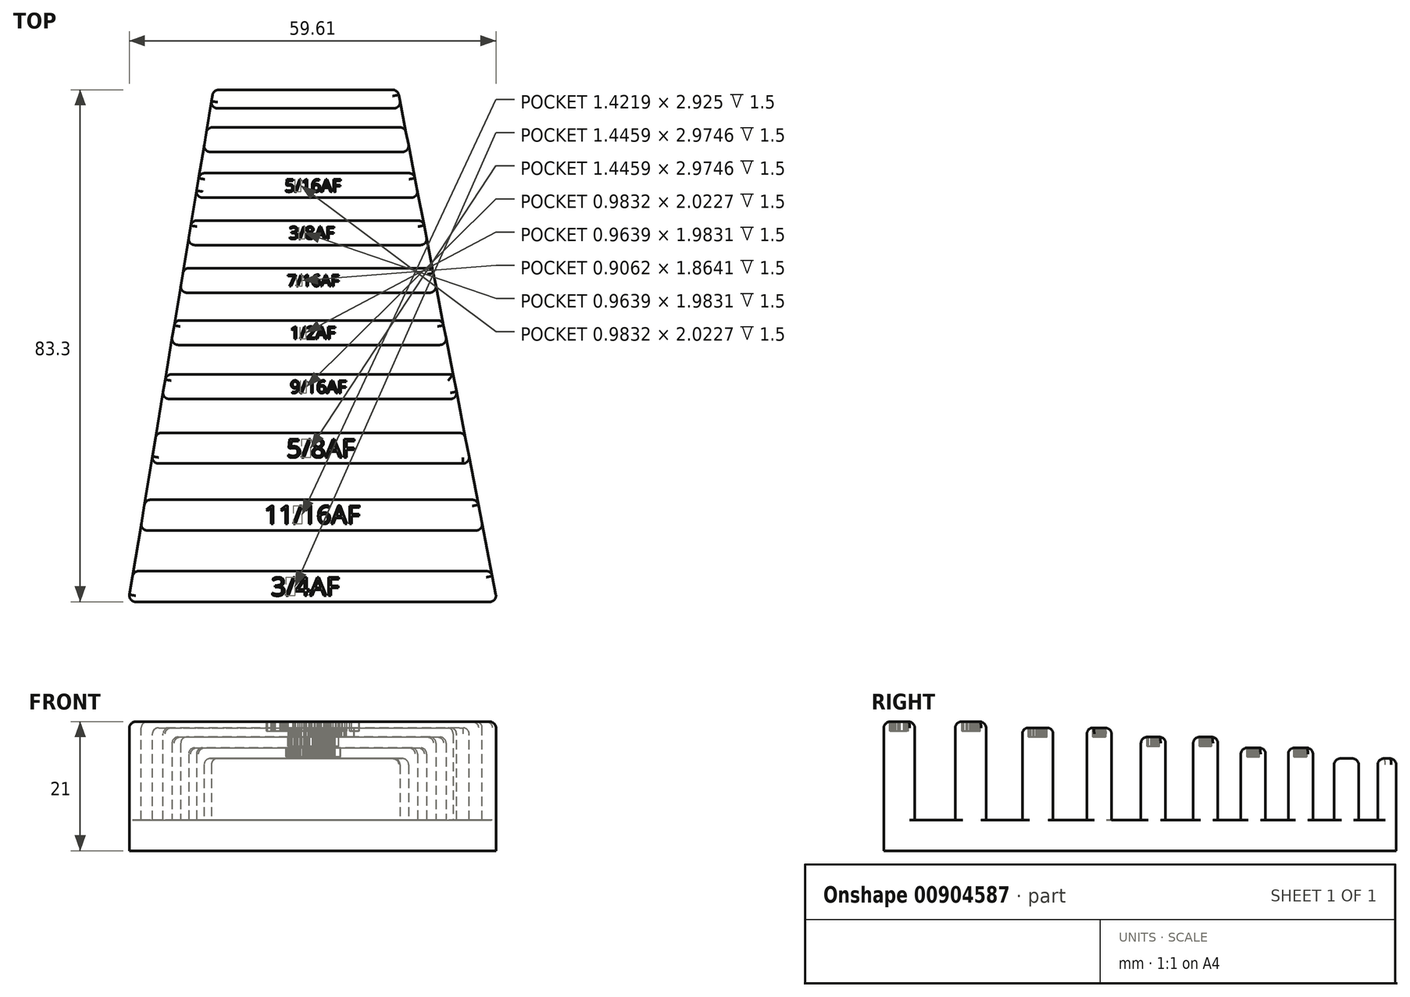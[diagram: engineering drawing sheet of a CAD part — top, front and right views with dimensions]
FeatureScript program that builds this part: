
annotation { "Feature Type Name" : "Feature", "Feature Type Description" : "" }
export const myFeature = defineFeature(function(context is Context, id is Id, definition is map)
    precondition{}
    {
        {
            var Q0;
            Q0=qCreatedBy(makeId("Top.planeOp"),FACE);
            var sketch = newSketch(context, id + "F0", { "sketchPlane" : qUnion([Q0])});
            skLineSegment(sketch, "E0.top", {"start": v(-30, -26.46) * mm, "end": v(30, -26.46) * mm});
            skLineSegment(sketch, "E1", {"start": v(-30, -26.46) * mm, "end": v(-16.18, 56.84) * mm});
            skLineSegment(sketch, "E2", {"start": v(-16.18, 56.84) * mm, "end": v(13.82, 56.84) * mm});
            skLineSegment(sketch, "E3", {"start": v(13.82, 56.84) * mm, "end": v(30, -26.46) * mm});
            skSolve(sketch);
        }
        {
            var Q0;
            Q0=qSketchRegion(id+"F0",true);
            extrude(context, id + "F1", {"entities" : qUnion([Q0]), "depth" : 5 * mm, "offsetDistance" : 25 * mm});
        }
        {
            var Q0;
            Q0=makeQuery(id+"F1.opExtrude","CAP_FACE",FACE,{"disambiguationData":[OSD([sQuery(id+"F0.wireOp",EDGE,"E0.top"),sQuery(id+"F0.wireOp",EDGE,"E1"),sQuery(id+"F0.wireOp",EDGE,"E2"),sQuery(id+"F0.wireOp",EDGE,"E3")])],"isStart":false});
            var sketch = newSketch(context, id + "F2", { "sketchPlane" : qUnion([Q0])});
            skLineSegment(sketch, "E4", {"start": v(-16.18, 56.84) * mm, "end": v(13.82, 56.84) * mm});
            skLineSegment(sketch, "E5", {"start": v(13.82, 56.84) * mm, "end": v(14.4, 53.84) * mm});
            skLineSegment(sketch, "E6", {"start": v(14.4, 53.84) * mm, "end": v(-16.68, 53.84) * mm});
            skLineSegment(sketch, "E7", {"start": v(-16.68, 53.84) * mm, "end": v(-16.18, 56.84) * mm});
            skLineSegment(sketch, "E8", {"start": v(-17.2, 50.74) * mm, "end": v(15, 50.74) * mm});
            skLineSegment(sketch, "E9", {"start": v(15, 50.74) * mm, "end": v(15.78, 46.74) * mm});
            skLineSegment(sketch, "E10", {"start": v(15.78, 46.74) * mm, "end": v(-17.85, 46.74) * mm});
            skLineSegment(sketch, "E11", {"start": v(-17.85, 46.74) * mm, "end": v(-17.2, 50.74) * mm});
            skLineSegment(sketch, "E12", {"start": v(-18.43, 43.3) * mm, "end": v(16.45, 43.3) * mm});
            skLineSegment(sketch, "E13", {"start": v(16.45, 43.3) * mm, "end": v(17.23, 39.3) * mm});
            skLineSegment(sketch, "E14", {"start": v(17.23, 39.3) * mm, "end": v(-19.1, 39.3) * mm});
            skLineSegment(sketch, "E15", {"start": v(-19.1, 39.3) * mm, "end": v(-18.43, 43.3) * mm});
            skLineSegment(sketch, "E16", {"start": v(-19.7, 35.6) * mm, "end": v(17.95, 35.6) * mm});
            skLineSegment(sketch, "E17", {"start": v(17.95, 35.6) * mm, "end": v(18.73, 31.6) * mm});
            skLineSegment(sketch, "E18", {"start": v(18.73, 31.6) * mm, "end": v(-20.37, 31.6) * mm});
            skLineSegment(sketch, "E19", {"start": v(-20.37, 31.6) * mm, "end": v(-19.7, 35.6) * mm});
            skLineSegment(sketch, "E20", {"start": v(-21, 27.84) * mm, "end": v(19.45, 27.84) * mm});
            skLineSegment(sketch, "E21", {"start": v(19.45, 27.84) * mm, "end": v(20.23, 23.84) * mm});
            skLineSegment(sketch, "E22", {"start": v(20.23, 23.84) * mm, "end": v(-21.65, 23.84) * mm});
            skLineSegment(sketch, "E23", {"start": v(-21.65, 23.84) * mm, "end": v(-21, 27.84) * mm});
            skLineSegment(sketch, "E24", {"start": v(-22.4, 19.34) * mm, "end": v(21.1, 19.34) * mm});
            skLineSegment(sketch, "E25", {"start": v(21.1, 19.34) * mm, "end": v(21.88, 15.34) * mm});
            skLineSegment(sketch, "E26", {"start": v(21.88, 15.34) * mm, "end": v(-23.06, 15.34) * mm});
            skLineSegment(sketch, "E27", {"start": v(-23.06, 15.34) * mm, "end": v(-22.4, 19.34) * mm});
            skLineSegment(sketch, "E28", {"start": v(-23.86, 10.54) * mm, "end": v(22.81, 10.54) * mm});
            skLineSegment(sketch, "E29", {"start": v(-24.52, 6.54) * mm, "end": v(23.6, 6.54) * mm});
            skLineSegment(sketch, "E30", {"start": v(24.66, 1.04) * mm, "end": v(-25.44, 1.04) * mm});
            skLineSegment(sketch, "E31", {"start": v(-26.27, -3.96) * mm, "end": v(25.63, -3.96) * mm});
            skLineSegment(sketch, "E32", {"start": v(26.78, -9.86) * mm, "end": v(-27.25, -9.86) * mm});
            skLineSegment(sketch, "E33", {"start": v(-28.08, -14.86) * mm, "end": v(27.75, -14.86) * mm});
            skLineSegment(sketch, "E34", {"start": v(29.03, -21.46) * mm, "end": v(-29.17, -21.46) * mm});
            skLineSegment(sketch, "E35", {"start": v(22.81, 10.54) * mm, "end": v(23.6, 6.54) * mm});
            skLineSegment(sketch, "E36", {"start": v(-24.52, 6.54) * mm, "end": v(-23.86, 10.54) * mm});
            skLineSegment(sketch, "E37", {"start": v(24.66, 1.04) * mm, "end": v(25.63, -3.96) * mm});
            skLineSegment(sketch, "E38", {"start": v(26.78, -9.86) * mm, "end": v(27.75, -14.86) * mm});
            skLineSegment(sketch, "E39", {"start": v(-28.08, -14.86) * mm, "end": v(-27.25, -9.86) * mm});
            skLineSegment(sketch, "E40", {"start": v(-26.27, -3.96) * mm, "end": v(-25.44, 1.04) * mm});
            skLineSegment(sketch, "E41", {"start": v(29.03, -21.46) * mm, "end": v(30, -26.46) * mm});
            skLineSegment(sketch, "E42", {"start": v(30, -26.46) * mm, "end": v(-30, -26.46) * mm});
            skLineSegment(sketch, "E43", {"start": v(-30, -26.46) * mm, "end": v(-29.17, -21.46) * mm});
            skSolve(sketch);
        }
        {
            var Q0;
            Q0=qSketchRegion(id+"F2",true);
            extrude(context, id + "F3", {"entities" : qUnion([Q0]), "operationType" : NewBodyOperationType.ADD, "depth" : 10 * mm, "offsetDistance" : 25 * mm});
        }
        {
            var Q0;
            Q0=makeQuery(id+"F3.opExtrude","CAP_FACE",FACE,{"disambiguationData":[OSD([sQuery(id+"F2.wireOp",EDGE,"E34"),sQuery(id+"F2.wireOp",EDGE,"E41"),sQuery(id+"F2.wireOp",EDGE,"E42"),sQuery(id+"F2.wireOp",EDGE,"E43")])],"isStart":false});
            extrude(context, id + "F4", {"entities" : qUnion([Q0]), "operationType" : NewBodyOperationType.ADD, "depth" : 6 * mm, "offsetDistance" : 25 * mm});
        }
        {
            var Q0;
            Q0=makeQuery(id+"F3.opExtrude","CAP_FACE",FACE,{"disambiguationData":[OSD([sQuery(id+"F2.wireOp",EDGE,"E32"),sQuery(id+"F2.wireOp",EDGE,"E33"),sQuery(id+"F2.wireOp",EDGE,"E38"),sQuery(id+"F2.wireOp",EDGE,"E39")])],"isStart":false});
            extrude(context, id + "F5", {"entities" : qUnion([Q0]), "operationType" : NewBodyOperationType.ADD, "depth" : 6 * mm, "offsetDistance" : 25 * mm});
        }
        {
            var Q0;
            Q0=makeQuery(id+"F3.opExtrude","CAP_FACE",FACE,{"disambiguationData":[OSD([sQuery(id+"F2.wireOp",EDGE,"E30"),sQuery(id+"F2.wireOp",EDGE,"E31"),sQuery(id+"F2.wireOp",EDGE,"E37"),sQuery(id+"F2.wireOp",EDGE,"E40")])],"isStart":false});
            var Q1;
            Q1=makeQuery(id+"F3.opExtrude","CAP_FACE",FACE,{"disambiguationData":[OSD([sQuery(id+"F2.wireOp",EDGE,"E28"),sQuery(id+"F2.wireOp",EDGE,"E29"),sQuery(id+"F2.wireOp",EDGE,"E35"),sQuery(id+"F2.wireOp",EDGE,"E36")])],"isStart":false});
            extrude(context, id + "F6", {"entities" : qUnion([Q0, Q1]), "operationType" : NewBodyOperationType.ADD, "depth" : 5 * mm, "offsetDistance" : 25 * mm});
        }
        {
            var Q0;
            Q0=makeQuery(id+"F3.opExtrude","CAP_FACE",FACE,{"disambiguationData":[OSD([sQuery(id+"F2.wireOp",EDGE,"E20"),sQuery(id+"F2.wireOp",EDGE,"E21"),sQuery(id+"F2.wireOp",EDGE,"E22"),sQuery(id+"F2.wireOp",EDGE,"E23")])],"isStart":false});
            var Q1;
            Q1=makeQuery(id+"F3.opExtrude","CAP_FACE",FACE,{"disambiguationData":[OSD([sQuery(id+"F2.wireOp",EDGE,"E24"),sQuery(id+"F2.wireOp",EDGE,"E25"),sQuery(id+"F2.wireOp",EDGE,"E26"),sQuery(id+"F2.wireOp",EDGE,"E27")])],"isStart":false});
            extrude(context, id + "F7", {"entities" : qUnion([Q0, Q1]), "operationType" : NewBodyOperationType.ADD, "depth" : 3.5 * mm, "offsetDistance" : 25 * mm});
        }
        {
            var Q0;
            Q0=makeQuery(id+"F3.opExtrude","CAP_FACE",FACE,{"disambiguationData":[OSD([sQuery(id+"F2.wireOp",EDGE,"E16"),sQuery(id+"F2.wireOp",EDGE,"E17"),sQuery(id+"F2.wireOp",EDGE,"E18"),sQuery(id+"F2.wireOp",EDGE,"E19")])],"isStart":false});
            var Q1;
            Q1=makeQuery(id+"F3.opExtrude","CAP_FACE",FACE,{"disambiguationData":[OSD([sQuery(id+"F2.wireOp",EDGE,"E12"),sQuery(id+"F2.wireOp",EDGE,"E13"),sQuery(id+"F2.wireOp",EDGE,"E14"),sQuery(id+"F2.wireOp",EDGE,"E15")])],"isStart":false});
            extrude(context, id + "F8", {"entities" : qUnion([Q0, Q1]), "operationType" : NewBodyOperationType.ADD, "depth" : 1.75 * mm, "offsetDistance" : 25 * mm});
        }
        {
            var Q0;
            Q0=makeQuery(id+"F3.opExtrude","CAP_EDGE",EDGE,{"disambiguationData":[OSD([sQuery(id+"F2.wireOp",EDGE,"E4")])],"isStart":false});
            var Q1;
            Q1=makeQuery(id+"F3.opExtrude","CAP_EDGE",EDGE,{"disambiguationData":[OSD([sQuery(id+"F2.wireOp",EDGE,"E8")])],"isStart":false});
            var Q2;
            Q2=makeQuery(id+"F3.opExtrude","CAP_EDGE",EDGE,{"disambiguationData":[OSD([sQuery(id+"F2.wireOp",EDGE,"E6")])],"isStart":false});
            var Q3;
            Q3=makeQuery(id+"F3.opExtrude","CAP_EDGE",EDGE,{"disambiguationData":[OSD([sQuery(id+"F2.wireOp",EDGE,"E7")])],"isStart":false});
            var Q4;
            Q4=makeQuery(id+"F3.opExtrude","CAP_EDGE",EDGE,{"disambiguationData":[OSD([sQuery(id+"F2.wireOp",EDGE,"E11")])],"isStart":false});
            var Q5;
            Q5=makeQuery(id+"F3.opExtrude","CAP_EDGE",EDGE,{"disambiguationData":[OSD([sQuery(id+"F2.wireOp",EDGE,"E10")])],"isStart":false});
            var Q6;
            Q6=makeQuery(id+"F8.opExtrude","CAP_EDGE",EDGE,{"disambiguationData":[OSD([sQuery(id+"F2.wireOp",EDGE,"E15")])],"isStart":false});
            var Q7;
            Q7=makeQuery(id+"F8.opExtrude","CAP_EDGE",EDGE,{"disambiguationData":[OSD([sQuery(id+"F2.wireOp",EDGE,"E12")])],"isStart":false});
            var Q8;
            Q8=makeQuery(id+"F8.opExtrude","CAP_EDGE",EDGE,{"disambiguationData":[OSD([sQuery(id+"F2.wireOp",EDGE,"E14")])],"isStart":false});
            var Q9;
            {var subQ0=sQuery(id+"F2.wireOp",EDGE,"E15");var subQ1=sQuery(id+"F2.wireOp",EDGE,"E14");var subQ2=sQuery(id+"F0.wireOp",EDGE,"E1");Q9=makeQuery(id+"F8.boolean.opBoolean","MERGE",EDGE,{"derivedFrom":[makeQuery(id+"F3.opExtrude","SWEPT_EDGE",EDGE,{"disambiguationData":[OSD([subQ2,subQ1,subQ0])]}),makeQuery(id+"F8.opExtrude","SWEPT_EDGE",EDGE,{"disambiguationData":[OSD([subQ2,subQ1,subQ0])]})]});}
            var Q10;
            {var subQ0=sQuery(id+"F2.wireOp",EDGE,"E15");var subQ1=sQuery(id+"F2.wireOp",EDGE,"E12");var subQ2=sQuery(id+"F0.wireOp",EDGE,"E1");Q10=makeQuery(id+"F8.boolean.opBoolean","MERGE",EDGE,{"derivedFrom":[makeQuery(id+"F3.opExtrude","SWEPT_EDGE",EDGE,{"disambiguationData":[OSD([subQ2,subQ1,subQ0])]}),makeQuery(id+"F8.opExtrude","SWEPT_EDGE",EDGE,{"disambiguationData":[OSD([subQ2,subQ1,subQ0])]})]});}
            var Q11;
            Q11=makeQuery(id+"F3.opExtrude","SWEPT_EDGE",EDGE,{"disambiguationData":[OSD([sQuery(id+"F0.wireOp",EDGE,"E1"),sQuery(id+"F2.wireOp",EDGE,"E6"),sQuery(id+"F2.wireOp",EDGE,"E7")])]});
            var Q12;
            Q12=makeQuery(id+"F3.boolean.opBoolean","MERGE",EDGE,{"derivedFrom":[makeQuery(id+"F1.opExtrude","SWEPT_EDGE",EDGE,{"disambiguationData":[OSD([sQuery(id+"F0.wireOp",EDGE,"E1"),sQuery(id+"F0.wireOp",EDGE,"E2")])]}),makeQuery(id+"F3.opExtrude","SWEPT_EDGE",EDGE,{"disambiguationData":[OSD([sQuery(id+"F2.wireOp",EDGE,"E4"),sQuery(id+"F2.wireOp",EDGE,"E7")])]})]});
            var Q13;
            Q13=makeQuery(id+"F3.opExtrude","SWEPT_EDGE",EDGE,{"disambiguationData":[OSD([sQuery(id+"F0.wireOp",EDGE,"E1"),sQuery(id+"F2.wireOp",EDGE,"E8"),sQuery(id+"F2.wireOp",EDGE,"E11")])]});
            var Q14;
            Q14=makeQuery(id+"F3.opExtrude","SWEPT_EDGE",EDGE,{"disambiguationData":[OSD([sQuery(id+"F0.wireOp",EDGE,"E1"),sQuery(id+"F2.wireOp",EDGE,"E10"),sQuery(id+"F2.wireOp",EDGE,"E11")])]});
            var Q15;
            {var subQ0=sQuery(id+"F2.wireOp",EDGE,"E19");var subQ1=sQuery(id+"F2.wireOp",EDGE,"E16");var subQ2=sQuery(id+"F0.wireOp",EDGE,"E1");Q15=makeQuery(id+"F8.boolean.opBoolean","MERGE",EDGE,{"derivedFrom":[makeQuery(id+"F3.opExtrude","SWEPT_EDGE",EDGE,{"disambiguationData":[OSD([subQ2,subQ1,subQ0])]}),makeQuery(id+"F8.opExtrude","SWEPT_EDGE",EDGE,{"disambiguationData":[OSD([subQ2,subQ1,subQ0])]})]});}
            var Q16;
            Q16=makeQuery(id+"F8.opExtrude","CAP_EDGE",EDGE,{"disambiguationData":[OSD([sQuery(id+"F2.wireOp",EDGE,"E16")])],"isStart":false});
            var Q17;
            Q17=makeQuery(id+"F8.opExtrude","CAP_EDGE",EDGE,{"disambiguationData":[OSD([sQuery(id+"F2.wireOp",EDGE,"E18")])],"isStart":false});
            var Q18;
            {var subQ0=sQuery(id+"F2.wireOp",EDGE,"E19");var subQ1=sQuery(id+"F2.wireOp",EDGE,"E18");var subQ2=sQuery(id+"F0.wireOp",EDGE,"E1");Q18=makeQuery(id+"F8.boolean.opBoolean","MERGE",EDGE,{"derivedFrom":[makeQuery(id+"F3.opExtrude","SWEPT_EDGE",EDGE,{"disambiguationData":[OSD([subQ2,subQ1,subQ0])]}),makeQuery(id+"F8.opExtrude","SWEPT_EDGE",EDGE,{"disambiguationData":[OSD([subQ2,subQ1,subQ0])]})]});}
            var Q19;
            Q19=makeQuery(id+"F8.opExtrude","CAP_EDGE",EDGE,{"disambiguationData":[OSD([sQuery(id+"F2.wireOp",EDGE,"E19")])],"isStart":false});
            var Q20;
            Q20=makeQuery(id+"F7.opExtrude","CAP_EDGE",EDGE,{"disambiguationData":[OSD([sQuery(id+"F2.wireOp",EDGE,"E23")])],"isStart":false});
            var Q21;
            {var subQ0=sQuery(id+"F2.wireOp",EDGE,"E23");var subQ1=sQuery(id+"F2.wireOp",EDGE,"E20");var subQ2=sQuery(id+"F0.wireOp",EDGE,"E1");Q21=makeQuery(id+"F7.boolean.opBoolean","MERGE",EDGE,{"derivedFrom":[makeQuery(id+"F3.opExtrude","SWEPT_EDGE",EDGE,{"disambiguationData":[OSD([subQ2,subQ1,subQ0])]}),makeQuery(id+"F7.opExtrude","SWEPT_EDGE",EDGE,{"disambiguationData":[OSD([subQ2,subQ1,subQ0])]})]});}
            var Q22;
            Q22=makeQuery(id+"F7.opExtrude","CAP_EDGE",EDGE,{"disambiguationData":[OSD([sQuery(id+"F2.wireOp",EDGE,"E20")])],"isStart":false});
            var Q23;
            Q23=makeQuery(id+"F7.opExtrude","CAP_EDGE",EDGE,{"disambiguationData":[OSD([sQuery(id+"F2.wireOp",EDGE,"E22")])],"isStart":false});
            var Q24;
            {var subQ0=sQuery(id+"F2.wireOp",EDGE,"E23");var subQ1=sQuery(id+"F2.wireOp",EDGE,"E22");var subQ2=sQuery(id+"F0.wireOp",EDGE,"E1");Q24=makeQuery(id+"F7.boolean.opBoolean","MERGE",EDGE,{"derivedFrom":[makeQuery(id+"F3.opExtrude","SWEPT_EDGE",EDGE,{"disambiguationData":[OSD([subQ2,subQ1,subQ0])]}),makeQuery(id+"F7.opExtrude","SWEPT_EDGE",EDGE,{"disambiguationData":[OSD([subQ2,subQ1,subQ0])]})]});}
            var Q25;
            {var subQ0=sQuery(id+"F2.wireOp",EDGE,"E27");var subQ1=sQuery(id+"F2.wireOp",EDGE,"E24");var subQ2=sQuery(id+"F0.wireOp",EDGE,"E1");Q25=makeQuery(id+"F7.boolean.opBoolean","MERGE",EDGE,{"derivedFrom":[makeQuery(id+"F3.opExtrude","SWEPT_EDGE",EDGE,{"disambiguationData":[OSD([subQ2,subQ1,subQ0])]}),makeQuery(id+"F7.opExtrude","SWEPT_EDGE",EDGE,{"disambiguationData":[OSD([subQ2,subQ1,subQ0])]})]});}
            var Q26;
            Q26=makeQuery(id+"F7.opExtrude","CAP_EDGE",EDGE,{"disambiguationData":[OSD([sQuery(id+"F2.wireOp",EDGE,"E24")])],"isStart":false});
            var Q27;
            Q27=makeQuery(id+"F7.opExtrude","CAP_EDGE",EDGE,{"disambiguationData":[OSD([sQuery(id+"F2.wireOp",EDGE,"E27")])],"isStart":false});
            var Q28;
            Q28=makeQuery(id+"F7.opExtrude","CAP_EDGE",EDGE,{"disambiguationData":[OSD([sQuery(id+"F2.wireOp",EDGE,"E26")])],"isStart":false});
            var Q29;
            {var subQ0=sQuery(id+"F2.wireOp",EDGE,"E27");var subQ1=sQuery(id+"F2.wireOp",EDGE,"E26");var subQ2=sQuery(id+"F0.wireOp",EDGE,"E1");Q29=makeQuery(id+"F7.boolean.opBoolean","MERGE",EDGE,{"derivedFrom":[makeQuery(id+"F3.opExtrude","SWEPT_EDGE",EDGE,{"disambiguationData":[OSD([subQ2,subQ1,subQ0])]}),makeQuery(id+"F7.opExtrude","SWEPT_EDGE",EDGE,{"disambiguationData":[OSD([subQ2,subQ1,subQ0])]})]});}
            var Q30;
            {var subQ0=sQuery(id+"F2.wireOp",EDGE,"E36");var subQ1=sQuery(id+"F2.wireOp",EDGE,"E28");var subQ2=sQuery(id+"F0.wireOp",EDGE,"E1");Q30=makeQuery(id+"F6.boolean.opBoolean","MERGE",EDGE,{"derivedFrom":[makeQuery(id+"F3.opExtrude","SWEPT_EDGE",EDGE,{"disambiguationData":[OSD([subQ2,subQ1,subQ0])]}),makeQuery(id+"F6.opExtrude","SWEPT_EDGE",EDGE,{"disambiguationData":[OSD([subQ2,subQ1,subQ0])]})]});}
            var Q31;
            Q31=makeQuery(id+"F6.opExtrude","CAP_EDGE",EDGE,{"disambiguationData":[OSD([sQuery(id+"F2.wireOp",EDGE,"E28")])],"isStart":false});
            var Q32;
            Q32=makeQuery(id+"F6.opExtrude","CAP_EDGE",EDGE,{"disambiguationData":[OSD([sQuery(id+"F2.wireOp",EDGE,"E36")])],"isStart":false});
            var Q33;
            Q33=makeQuery(id+"F6.opExtrude","CAP_EDGE",EDGE,{"disambiguationData":[OSD([sQuery(id+"F2.wireOp",EDGE,"E29")])],"isStart":false});
            var Q34;
            {var subQ0=sQuery(id+"F2.wireOp",EDGE,"E36");var subQ1=sQuery(id+"F2.wireOp",EDGE,"E29");var subQ2=sQuery(id+"F0.wireOp",EDGE,"E1");Q34=makeQuery(id+"F6.boolean.opBoolean","MERGE",EDGE,{"derivedFrom":[makeQuery(id+"F3.opExtrude","SWEPT_EDGE",EDGE,{"disambiguationData":[OSD([subQ2,subQ1,subQ0])]}),makeQuery(id+"F6.opExtrude","SWEPT_EDGE",EDGE,{"disambiguationData":[OSD([subQ2,subQ1,subQ0])]})]});}
            var Q35;
            {var subQ0=sQuery(id+"F2.wireOp",EDGE,"E40");var subQ1=sQuery(id+"F2.wireOp",EDGE,"E30");var subQ2=sQuery(id+"F0.wireOp",EDGE,"E1");Q35=makeQuery(id+"F6.boolean.opBoolean","MERGE",EDGE,{"derivedFrom":[makeQuery(id+"F3.opExtrude","SWEPT_EDGE",EDGE,{"disambiguationData":[OSD([subQ2,subQ1,subQ0])]}),makeQuery(id+"F6.opExtrude","SWEPT_EDGE",EDGE,{"disambiguationData":[OSD([subQ2,subQ1,subQ0])]})]});}
            var Q36;
            Q36=makeQuery(id+"F6.opExtrude","CAP_EDGE",EDGE,{"disambiguationData":[OSD([sQuery(id+"F2.wireOp",EDGE,"E30")])],"isStart":false});
            var Q37;
            Q37=makeQuery(id+"F6.opExtrude","CAP_EDGE",EDGE,{"disambiguationData":[OSD([sQuery(id+"F2.wireOp",EDGE,"E40")])],"isStart":false});
            var Q38;
            Q38=makeQuery(id+"F6.opExtrude","CAP_EDGE",EDGE,{"disambiguationData":[OSD([sQuery(id+"F2.wireOp",EDGE,"E31")])],"isStart":false});
            var Q39;
            {var subQ0=sQuery(id+"F2.wireOp",EDGE,"E40");var subQ1=sQuery(id+"F2.wireOp",EDGE,"E31");var subQ2=sQuery(id+"F0.wireOp",EDGE,"E1");Q39=makeQuery(id+"F6.boolean.opBoolean","MERGE",EDGE,{"derivedFrom":[makeQuery(id+"F3.opExtrude","SWEPT_EDGE",EDGE,{"disambiguationData":[OSD([subQ2,subQ1,subQ0])]}),makeQuery(id+"F6.opExtrude","SWEPT_EDGE",EDGE,{"disambiguationData":[OSD([subQ2,subQ1,subQ0])]})]});}
            var Q40;
            {var subQ0=sQuery(id+"F2.wireOp",EDGE,"E39");var subQ1=sQuery(id+"F2.wireOp",EDGE,"E32");var subQ2=sQuery(id+"F0.wireOp",EDGE,"E1");Q40=makeQuery(id+"F5.boolean.opBoolean","MERGE",EDGE,{"derivedFrom":[makeQuery(id+"F3.opExtrude","SWEPT_EDGE",EDGE,{"disambiguationData":[OSD([subQ2,subQ1,subQ0])]}),makeQuery(id+"F5.opExtrude","SWEPT_EDGE",EDGE,{"disambiguationData":[OSD([subQ2,subQ1,subQ0])]})]});}
            var Q41;
            Q41=makeQuery(id+"F5.opExtrude","CAP_EDGE",EDGE,{"disambiguationData":[OSD([sQuery(id+"F2.wireOp",EDGE,"E32")])],"isStart":false});
            var Q42;
            Q42=makeQuery(id+"F5.opExtrude","CAP_EDGE",EDGE,{"disambiguationData":[OSD([sQuery(id+"F2.wireOp",EDGE,"E39")])],"isStart":false});
            var Q43;
            Q43=makeQuery(id+"F5.opExtrude","CAP_EDGE",EDGE,{"disambiguationData":[OSD([sQuery(id+"F2.wireOp",EDGE,"E33")])],"isStart":false});
            var Q44;
            {var subQ0=sQuery(id+"F2.wireOp",EDGE,"E39");var subQ1=sQuery(id+"F2.wireOp",EDGE,"E33");var subQ2=sQuery(id+"F0.wireOp",EDGE,"E1");Q44=makeQuery(id+"F5.boolean.opBoolean","MERGE",EDGE,{"derivedFrom":[makeQuery(id+"F3.opExtrude","SWEPT_EDGE",EDGE,{"disambiguationData":[OSD([subQ2,subQ1,subQ0])]}),makeQuery(id+"F5.opExtrude","SWEPT_EDGE",EDGE,{"disambiguationData":[OSD([subQ2,subQ1,subQ0])]})]});}
            var Q45;
            Q45=makeQuery(id+"F4.opExtrude","CAP_EDGE",EDGE,{"disambiguationData":[OSD([sQuery(id+"F2.wireOp",EDGE,"E34")])],"isStart":false});
            var Q46;
            {var subQ0=sQuery(id+"F2.wireOp",EDGE,"E43");var subQ1=sQuery(id+"F2.wireOp",EDGE,"E34");var subQ2=sQuery(id+"F0.wireOp",EDGE,"E1");Q46=makeQuery(id+"F4.boolean.opBoolean","MERGE",EDGE,{"derivedFrom":[makeQuery(id+"F3.opExtrude","SWEPT_EDGE",EDGE,{"disambiguationData":[OSD([subQ2,subQ1,subQ0])]}),makeQuery(id+"F4.opExtrude","SWEPT_EDGE",EDGE,{"disambiguationData":[OSD([subQ2,subQ1,subQ0])]})]});}
            var Q47;
            Q47=makeQuery(id+"F4.opExtrude","CAP_EDGE",EDGE,{"disambiguationData":[OSD([sQuery(id+"F2.wireOp",EDGE,"E43")])],"isStart":false});
            var Q48;
            Q48=makeQuery(id+"F4.opExtrude","CAP_EDGE",EDGE,{"disambiguationData":[OSD([sQuery(id+"F2.wireOp",EDGE,"E42")])],"isStart":false});
            var Q49;
            {var subQ0=sQuery(id+"F2.wireOp",EDGE,"E43");var subQ1=sQuery(id+"F2.wireOp",EDGE,"E42");Q49=makeQuery(id+"F4.boolean.opBoolean","MERGE",EDGE,{"derivedFrom":[makeQuery(id+"F3.boolean.opBoolean","MERGE",EDGE,{"derivedFrom":[makeQuery(id+"F1.opExtrude","SWEPT_EDGE",EDGE,{"disambiguationData":[OSD([sQuery(id+"F0.wireOp",EDGE,"E0.top"),sQuery(id+"F0.wireOp",EDGE,"E1")])]}),makeQuery(id+"F3.opExtrude","SWEPT_EDGE",EDGE,{"disambiguationData":[OSD([subQ1,subQ0])]})]}),makeQuery(id+"F4.opExtrude","SWEPT_EDGE",EDGE,{"disambiguationData":[OSD([subQ1,subQ0])]})]});}
            var Q50;
            Q50=makeQuery(id+"F4.opExtrude","CAP_EDGE",EDGE,{"disambiguationData":[OSD([sQuery(id+"F2.wireOp",EDGE,"E41")])],"isStart":false});
            var Q51;
            {var subQ0=sQuery(id+"F2.wireOp",EDGE,"E38");var subQ1=sQuery(id+"F2.wireOp",EDGE,"E33");var subQ2=sQuery(id+"F0.wireOp",EDGE,"E3");Q51=makeQuery(id+"F5.boolean.opBoolean","MERGE",EDGE,{"derivedFrom":[makeQuery(id+"F3.opExtrude","SWEPT_EDGE",EDGE,{"disambiguationData":[OSD([subQ2,subQ1,subQ0])]}),makeQuery(id+"F5.opExtrude","SWEPT_EDGE",EDGE,{"disambiguationData":[OSD([subQ2,subQ1,subQ0])]})]});}
            var Q52;
            Q52=makeQuery(id+"F5.opExtrude","CAP_EDGE",EDGE,{"disambiguationData":[OSD([sQuery(id+"F2.wireOp",EDGE,"E38")])],"isStart":false});
            var Q53;
            {var subQ0=sQuery(id+"F2.wireOp",EDGE,"E38");var subQ1=sQuery(id+"F2.wireOp",EDGE,"E32");var subQ2=sQuery(id+"F0.wireOp",EDGE,"E3");Q53=makeQuery(id+"F5.boolean.opBoolean","MERGE",EDGE,{"derivedFrom":[makeQuery(id+"F3.opExtrude","SWEPT_EDGE",EDGE,{"disambiguationData":[OSD([subQ2,subQ1,subQ0])]}),makeQuery(id+"F5.opExtrude","SWEPT_EDGE",EDGE,{"disambiguationData":[OSD([subQ2,subQ1,subQ0])]})]});}
            var Q54;
            {var subQ0=sQuery(id+"F2.wireOp",EDGE,"E37");var subQ1=sQuery(id+"F2.wireOp",EDGE,"E31");var subQ2=sQuery(id+"F0.wireOp",EDGE,"E3");Q54=makeQuery(id+"F6.boolean.opBoolean","MERGE",EDGE,{"derivedFrom":[makeQuery(id+"F3.opExtrude","SWEPT_EDGE",EDGE,{"disambiguationData":[OSD([subQ2,subQ1,subQ0])]}),makeQuery(id+"F6.opExtrude","SWEPT_EDGE",EDGE,{"disambiguationData":[OSD([subQ2,subQ1,subQ0])]})]});}
            var Q55;
            Q55=makeQuery(id+"F6.opExtrude","CAP_EDGE",EDGE,{"disambiguationData":[OSD([sQuery(id+"F2.wireOp",EDGE,"E37")])],"isStart":false});
            var Q56;
            {var subQ0=sQuery(id+"F2.wireOp",EDGE,"E37");var subQ1=sQuery(id+"F2.wireOp",EDGE,"E30");var subQ2=sQuery(id+"F0.wireOp",EDGE,"E3");Q56=makeQuery(id+"F6.boolean.opBoolean","MERGE",EDGE,{"derivedFrom":[makeQuery(id+"F3.opExtrude","SWEPT_EDGE",EDGE,{"disambiguationData":[OSD([subQ2,subQ1,subQ0])]}),makeQuery(id+"F6.opExtrude","SWEPT_EDGE",EDGE,{"disambiguationData":[OSD([subQ2,subQ1,subQ0])]})]});}
            var Q57;
            {var subQ0=sQuery(id+"F2.wireOp",EDGE,"E35");var subQ1=sQuery(id+"F2.wireOp",EDGE,"E29");var subQ2=sQuery(id+"F0.wireOp",EDGE,"E3");Q57=makeQuery(id+"F6.boolean.opBoolean","MERGE",EDGE,{"derivedFrom":[makeQuery(id+"F3.opExtrude","SWEPT_EDGE",EDGE,{"disambiguationData":[OSD([subQ2,subQ1,subQ0])]}),makeQuery(id+"F6.opExtrude","SWEPT_EDGE",EDGE,{"disambiguationData":[OSD([subQ2,subQ1,subQ0])]})]});}
            var Q58;
            Q58=makeQuery(id+"F6.opExtrude","CAP_EDGE",EDGE,{"disambiguationData":[OSD([sQuery(id+"F2.wireOp",EDGE,"E35")])],"isStart":false});
            var Q59;
            {var subQ0=sQuery(id+"F2.wireOp",EDGE,"E26");var subQ1=sQuery(id+"F2.wireOp",EDGE,"E25");var subQ2=sQuery(id+"F0.wireOp",EDGE,"E3");Q59=makeQuery(id+"F7.boolean.opBoolean","MERGE",EDGE,{"derivedFrom":[makeQuery(id+"F3.opExtrude","SWEPT_EDGE",EDGE,{"disambiguationData":[OSD([subQ2,subQ1,subQ0])]}),makeQuery(id+"F7.opExtrude","SWEPT_EDGE",EDGE,{"disambiguationData":[OSD([subQ2,subQ1,subQ0])]})]});}
            var Q60;
            Q60=makeQuery(id+"F7.opExtrude","CAP_EDGE",EDGE,{"disambiguationData":[OSD([sQuery(id+"F2.wireOp",EDGE,"E25")])],"isStart":false});
            var Q61;
            {var subQ0=sQuery(id+"F2.wireOp",EDGE,"E25");var subQ1=sQuery(id+"F2.wireOp",EDGE,"E24");var subQ2=sQuery(id+"F0.wireOp",EDGE,"E3");Q61=makeQuery(id+"F7.boolean.opBoolean","MERGE",EDGE,{"derivedFrom":[makeQuery(id+"F3.opExtrude","SWEPT_EDGE",EDGE,{"disambiguationData":[OSD([subQ2,subQ1,subQ0])]}),makeQuery(id+"F7.opExtrude","SWEPT_EDGE",EDGE,{"disambiguationData":[OSD([subQ2,subQ1,subQ0])]})]});}
            var Q62;
            {var subQ0=sQuery(id+"F2.wireOp",EDGE,"E22");var subQ1=sQuery(id+"F2.wireOp",EDGE,"E21");var subQ2=sQuery(id+"F0.wireOp",EDGE,"E3");Q62=makeQuery(id+"F7.boolean.opBoolean","MERGE",EDGE,{"derivedFrom":[makeQuery(id+"F3.opExtrude","SWEPT_EDGE",EDGE,{"disambiguationData":[OSD([subQ2,subQ1,subQ0])]}),makeQuery(id+"F7.opExtrude","SWEPT_EDGE",EDGE,{"disambiguationData":[OSD([subQ2,subQ1,subQ0])]})]});}
            var Q63;
            Q63=makeQuery(id+"F7.opExtrude","CAP_EDGE",EDGE,{"disambiguationData":[OSD([sQuery(id+"F2.wireOp",EDGE,"E21")])],"isStart":false});
            var Q64;
            {var subQ0=sQuery(id+"F2.wireOp",EDGE,"E18");var subQ1=sQuery(id+"F2.wireOp",EDGE,"E17");var subQ2=sQuery(id+"F0.wireOp",EDGE,"E3");Q64=makeQuery(id+"F8.boolean.opBoolean","MERGE",EDGE,{"derivedFrom":[makeQuery(id+"F3.opExtrude","SWEPT_EDGE",EDGE,{"disambiguationData":[OSD([subQ2,subQ1,subQ0])]}),makeQuery(id+"F8.opExtrude","SWEPT_EDGE",EDGE,{"disambiguationData":[OSD([subQ2,subQ1,subQ0])]})]});}
            var Q65;
            Q65=makeQuery(id+"F8.opExtrude","CAP_EDGE",EDGE,{"disambiguationData":[OSD([sQuery(id+"F2.wireOp",EDGE,"E17")])],"isStart":false});
            var Q66;
            {var subQ0=sQuery(id+"F2.wireOp",EDGE,"E17");var subQ1=sQuery(id+"F2.wireOp",EDGE,"E16");var subQ2=sQuery(id+"F0.wireOp",EDGE,"E3");Q66=makeQuery(id+"F8.boolean.opBoolean","MERGE",EDGE,{"derivedFrom":[makeQuery(id+"F3.opExtrude","SWEPT_EDGE",EDGE,{"disambiguationData":[OSD([subQ2,subQ1,subQ0])]}),makeQuery(id+"F8.opExtrude","SWEPT_EDGE",EDGE,{"disambiguationData":[OSD([subQ2,subQ1,subQ0])]})]});}
            var Q67;
            {var subQ0=sQuery(id+"F2.wireOp",EDGE,"E14");var subQ1=sQuery(id+"F2.wireOp",EDGE,"E13");var subQ2=sQuery(id+"F0.wireOp",EDGE,"E3");Q67=makeQuery(id+"F8.boolean.opBoolean","MERGE",EDGE,{"derivedFrom":[makeQuery(id+"F3.opExtrude","SWEPT_EDGE",EDGE,{"disambiguationData":[OSD([subQ2,subQ1,subQ0])]}),makeQuery(id+"F8.opExtrude","SWEPT_EDGE",EDGE,{"disambiguationData":[OSD([subQ2,subQ1,subQ0])]})]});}
            var Q68;
            Q68=makeQuery(id+"F8.opExtrude","CAP_EDGE",EDGE,{"disambiguationData":[OSD([sQuery(id+"F2.wireOp",EDGE,"E13")])],"isStart":false});
            var Q69;
            {var subQ0=sQuery(id+"F2.wireOp",EDGE,"E13");var subQ1=sQuery(id+"F2.wireOp",EDGE,"E12");var subQ2=sQuery(id+"F0.wireOp",EDGE,"E3");Q69=makeQuery(id+"F8.boolean.opBoolean","MERGE",EDGE,{"derivedFrom":[makeQuery(id+"F3.opExtrude","SWEPT_EDGE",EDGE,{"disambiguationData":[OSD([subQ2,subQ1,subQ0])]}),makeQuery(id+"F8.opExtrude","SWEPT_EDGE",EDGE,{"disambiguationData":[OSD([subQ2,subQ1,subQ0])]})]});}
            var Q70;
            Q70=makeQuery(id+"F3.opExtrude","SWEPT_EDGE",EDGE,{"disambiguationData":[OSD([sQuery(id+"F0.wireOp",EDGE,"E3"),sQuery(id+"F2.wireOp",EDGE,"E9"),sQuery(id+"F2.wireOp",EDGE,"E10")])]});
            var Q71;
            Q71=makeQuery(id+"F3.opExtrude","CAP_EDGE",EDGE,{"disambiguationData":[OSD([sQuery(id+"F2.wireOp",EDGE,"E9")])],"isStart":false});
            var Q72;
            Q72=makeQuery(id+"F3.opExtrude","SWEPT_EDGE",EDGE,{"disambiguationData":[OSD([sQuery(id+"F0.wireOp",EDGE,"E3"),sQuery(id+"F2.wireOp",EDGE,"E8"),sQuery(id+"F2.wireOp",EDGE,"E9")])]});
            var Q73;
            Q73=makeQuery(id+"F3.opExtrude","SWEPT_EDGE",EDGE,{"disambiguationData":[OSD([sQuery(id+"F0.wireOp",EDGE,"E3"),sQuery(id+"F2.wireOp",EDGE,"E5"),sQuery(id+"F2.wireOp",EDGE,"E6")])]});
            var Q74;
            Q74=makeQuery(id+"F3.boolean.opBoolean","MERGE",EDGE,{"derivedFrom":[makeQuery(id+"F1.opExtrude","SWEPT_EDGE",EDGE,{"disambiguationData":[OSD([sQuery(id+"F0.wireOp",EDGE,"E2"),sQuery(id+"F0.wireOp",EDGE,"E3")])]}),makeQuery(id+"F3.opExtrude","SWEPT_EDGE",EDGE,{"disambiguationData":[OSD([sQuery(id+"F2.wireOp",EDGE,"E4"),sQuery(id+"F2.wireOp",EDGE,"E5")])]})]});
            var Q75;
            Q75=makeQuery(id+"F3.opExtrude","CAP_EDGE",EDGE,{"disambiguationData":[OSD([sQuery(id+"F2.wireOp",EDGE,"E5")])],"isStart":false});
            var Q76;
            {var subQ0=sQuery(id+"F2.wireOp",EDGE,"E41");var subQ1=sQuery(id+"F2.wireOp",EDGE,"E34");var subQ2=sQuery(id+"F0.wireOp",EDGE,"E3");Q76=makeQuery(id+"F4.boolean.opBoolean","MERGE",EDGE,{"derivedFrom":[makeQuery(id+"F3.opExtrude","SWEPT_EDGE",EDGE,{"disambiguationData":[OSD([subQ2,subQ1,subQ0])]}),makeQuery(id+"F4.opExtrude","SWEPT_EDGE",EDGE,{"disambiguationData":[OSD([subQ2,subQ1,subQ0])]})]});}
            var Q77;
            {var subQ0=sQuery(id+"F2.wireOp",EDGE,"E42");var subQ1=sQuery(id+"F2.wireOp",EDGE,"E41");Q77=makeQuery(id+"F4.boolean.opBoolean","MERGE",EDGE,{"derivedFrom":[makeQuery(id+"F3.boolean.opBoolean","MERGE",EDGE,{"derivedFrom":[makeQuery(id+"F1.opExtrude","SWEPT_EDGE",EDGE,{"disambiguationData":[OSD([sQuery(id+"F0.wireOp",EDGE,"E0.top"),sQuery(id+"F0.wireOp",EDGE,"E3")])]}),makeQuery(id+"F3.opExtrude","SWEPT_EDGE",EDGE,{"disambiguationData":[OSD([subQ1,subQ0])]})]}),makeQuery(id+"F4.opExtrude","SWEPT_EDGE",EDGE,{"disambiguationData":[OSD([subQ1,subQ0])]})]});}
            var Q78;
            {var subQ0=sQuery(id+"F2.wireOp",EDGE,"E21");var subQ1=sQuery(id+"F2.wireOp",EDGE,"E20");var subQ2=sQuery(id+"F0.wireOp",EDGE,"E3");Q78=makeQuery(id+"F7.boolean.opBoolean","MERGE",EDGE,{"derivedFrom":[makeQuery(id+"F3.opExtrude","SWEPT_EDGE",EDGE,{"disambiguationData":[OSD([subQ2,subQ1,subQ0])]}),makeQuery(id+"F7.opExtrude","SWEPT_EDGE",EDGE,{"disambiguationData":[OSD([subQ2,subQ1,subQ0])]})]});}
            fillet(context, id + "F9", {"entities" : qUnion([Q0, Q1, Q2, Q3, Q4, Q5, Q6, Q7, Q8, Q9, Q10, Q11, Q12, Q13, Q14, Q15, Q16, Q17, Q18, Q19, Q20, Q21, Q22, Q23, Q24, Q25, Q26, Q27, Q28, Q29, Q30, Q31, Q32, Q33, Q34, Q35, Q36, Q37, Q38, Q39, Q40, Q41, Q42, Q43, Q44, Q45, Q46, Q47, Q48, Q49, Q50, Q51, Q52, Q53, Q54, Q55, Q56, Q57, Q58, Q59, Q60, Q61, Q62, Q63, Q64, Q65, Q66, Q67, Q68, Q69, Q70, Q71, Q72, Q73, Q74, Q75, Q76, Q77, Q78]), "radius" : 1 * mm, "tangentPropagation" : true, "allowEdgeOverflow" : false});
        }
        {
            var Q0;
            Q0=makeQuery(id+"F5.opExtrude","CAP_FACE",FACE,{"disambiguationData":[OSD([sQuery(id+"F2.wireOp",EDGE,"E32"),sQuery(id+"F2.wireOp",EDGE,"E33"),sQuery(id+"F2.wireOp",EDGE,"E38"),sQuery(id+"F2.wireOp",EDGE,"E39")])],"isStart":false});
            var sketch = newSketch(context, id + "F10", { "sketchPlane" : qUnion([Q0])});
            skText(sketch, "E44", { "text": "3/4AF", "fontName": "OpenSans-Regular.ttf"});
            skText(sketch, "E45", { "text": "11/16AF", "fontName": "OpenSans-Regular.ttf"});
            const initialGuessF10  = {"E44": [-0.00676, -0.02546, 1, 0, 0.003], "E45": [-0.00789, -0.01375, 1, 0, 0.00295]};
            skSetInitialGuess(sketch, initialGuessF10);
            skSolve(sketch);
        }
        {
            var Q0;
            Q0=qSketchRegion(id+"F10",true);
            extrude(context, id + "F11", {"entities" : qUnion([Q0]), "operationType" : NewBodyOperationType.REMOVE, "oppositeDirection" : true, "depth" : 1.5 * mm, "offsetDistance" : 25 * mm});
        }
        {
            var Q0;
            Q0=makeQuery(id+"F6.opExtrude","CAP_FACE",FACE,{"disambiguationData":[OSD([sQuery(id+"F2.wireOp",EDGE,"E30"),sQuery(id+"F2.wireOp",EDGE,"E31"),sQuery(id+"F2.wireOp",EDGE,"E37"),sQuery(id+"F2.wireOp",EDGE,"E40")])],"isStart":false});
            var sketch = newSketch(context, id + "F12", { "sketchPlane" : qUnion([Q0])});
            skText(sketch, "E46", { "text": "5/8AF", "fontName": "OpenSans-Regular.ttf"});
            skText(sketch, "E47", { "text": "9/16AF", "fontName": "OpenSans-Regular.ttf"});
            const initialGuessF12  = {"E46": [-0.00423, -0.00296, 1, 0, 0.003], "E47": [-0.00367, 0.00752, 1, 0, 0.00204]};
            skSetInitialGuess(sketch, initialGuessF12);
            skSolve(sketch);
        }
        {
            var Q0;
            Q0=qSketchRegion(id+"F12",true);
            extrude(context, id + "F13", {"entities" : qUnion([Q0]), "operationType" : NewBodyOperationType.REMOVE, "oppositeDirection" : true, "depth" : 1.5 * mm, "offsetDistance" : 25 * mm});
        }
        {
            var Q0;
            Q0=makeQuery(id+"F7.opExtrude","CAP_FACE",FACE,{"disambiguationData":[OSD([sQuery(id+"F2.wireOp",EDGE,"E24"),sQuery(id+"F2.wireOp",EDGE,"E25"),sQuery(id+"F2.wireOp",EDGE,"E26"),sQuery(id+"F2.wireOp",EDGE,"E27")])],"isStart":false});
            var sketch = newSketch(context, id + "F14", { "sketchPlane" : qUnion([Q0])});
            skText(sketch, "E48", { "text": "1/2AF", "fontName": "OpenSans-Regular.ttf"});
            skText(sketch, "E49", { "text": "7/16AF", "fontName": "OpenSans-Regular.ttf"});
            const initialGuessF14  = {"E48": [-0.00371, 0.01634, 1, 0, 0.002], "E49": [-0.00415, 0.02489, 1, 0, 0.00188]};
            skSetInitialGuess(sketch, initialGuessF14);
            skSolve(sketch);
        }
        {
            var Q0;
            Q0=qSketchRegion(id+"F14",true);
            extrude(context, id + "F15", {"entities" : qUnion([Q0]), "operationType" : NewBodyOperationType.REMOVE, "oppositeDirection" : true, "depth" : 1.5 * mm, "offsetDistance" : 25 * mm});
        }
        {
            var Q0;
            Q0=makeQuery(id+"F8.opExtrude","CAP_FACE",FACE,{"disambiguationData":[OSD([sQuery(id+"F2.wireOp",EDGE,"E16"),sQuery(id+"F2.wireOp",EDGE,"E17"),sQuery(id+"F2.wireOp",EDGE,"E18"),sQuery(id+"F2.wireOp",EDGE,"E19")])],"isStart":false});
            var sketch = newSketch(context, id + "F16", { "sketchPlane" : qUnion([Q0])});
            skText(sketch, "E50", { "text": "3/8AF", "fontName": "OpenSans-Regular.ttf"});
            skText(sketch, "E51", { "text": "5/16AF", "fontName": "OpenSans-Regular.ttf"});
            const initialGuessF16  = {"E50": [-0.00387, 0.0326, 1, 0, 0.002], "E51": [-0.00456, 0.04026, 1, 0, 0.00204]};
            skSetInitialGuess(sketch, initialGuessF16);
            skSolve(sketch);
        }
        {
            var Q0;
            Q0=qSketchRegion(id+"F16",true);
            extrude(context, id + "F17", {"entities" : qUnion([Q0]), "operationType" : NewBodyOperationType.REMOVE, "oppositeDirection" : true, "depth" : 1.5 * mm, "offsetDistance" : 25 * mm});
        }
    });
